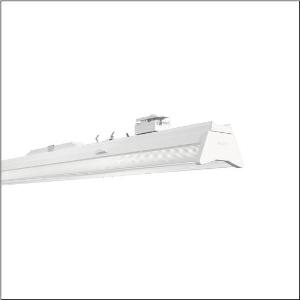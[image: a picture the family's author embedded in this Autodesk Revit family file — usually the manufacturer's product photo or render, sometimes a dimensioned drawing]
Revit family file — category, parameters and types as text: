
# Revit family: licross_r__21_performance_mo_52td16dn445g_3218
name_source: partatom
category: Lighting Fixtures
units: mm (PartAtom-declared; Revit-internal decimal feet)

## family parameters
Cut with Voids When Loaded = No
Host = Face
Light Source = No
Part Type = Normal
Room Calculation Point = No
Round Connector Dimension = Use Diameter
Shared = No

## types (1)
- --- (1 x LED, 4500 lm, 24.9 W, 4000K)
    Apparent Load = 25 VA
    CIE Flux Codes = 66 88 96 79 100
    Color Rendering = 80
    Color Temperature = 4000K
    Default Elevation = 1800 mm
    Description = Licross® 21 Performance MO, luminaire insert, of sheet steel, galvanised, coil coated, white, length: 1.500mm, width: 120mm, height: 123mm, LED rated luminous flux: 4.500lm, light colour: 840, SDCM (Standard Deviation of Colour Matching)MacAdam ≤ 3 SDCM (initial), control gear: DALI 2, with plug, 5-pole, with phase selection, mains connection: 220..240V, AC, 50/60Hz, rated input power: 25W, internal wiring halogen-free, primary light control with lens, of plastic, primary optical cover: cover, of PMMA, CAT 2 (L<= 3000cd/m²), light emission: direct/indirect distribution, primary light characteristic: symmetric, protection rating (complete): IP54, insulation class (complete): insulation class I (protective earthing), certification: CE, ENEC, VDE, UKCA, protection symbol: D if used in an environment with non-conductive dust loads with corresponding accessories, impact resistance: IK06, permissible ambient temperature for indoor applications: -25..+50°C, corresponds to IFS (International Featured Standards) requirements for safety and quality in the food industry, reducing of maximum allowable ambient temperature of 5°C with ceiling mounting, LABS conformity tested according to VDMA 24364:2018-05, packaging unit: 1 piece
    Height = 114 mm
    Lamp = 1 x LED
    Lamp Light Flux = 4500 lm
    Lamp Power = 24.9 W
    Lamp count = 1
    Length = 1500 mm
    Luminous efficacy = 181 lm/W
    Manufacturer = Siteco
    ModVariant = No
    Model = 52TD16DN445G
    Mounting Place = Ceiling
    Mounting Type = Pendant
    Number of Poles = 1
    OnlyDefault = Yes
    Power Factor = 1
    Product Name = Licross® 21 Performance MO
    Product group = luminaire insert | ceiling pendant
    ProductGroupID = 901
    Protection Class = Protection class I
    Protection Degree = IP 54
    RLX_Detail_Level = 1
    RLX_Emergency_Light_Flux = 0 lm
    RLX_Emergency_Type = 0
    RLX_Emergency_Type_DB = No
    RlxData = <blob elided: 33713 chars, md5=6601fcc0>
    Socket = socket
    Standby Power = 0 W
    System Light Flux = 4500 lm
    System Power = 25 W
    Type Comments = factory setting: luminous flux: 100 % | dim-lin: 254 | 165 mA
    Type Image = l_1256138.jpg
    URL = http://relux.com
    VarID = @adj_058747
    Voltage = 0 V
    Weight = 0.00 kg
    Width = 120 mm

## geometry (parser evidence)
native form markers: Blend x4, Sweep x14
no freeform markers — native parametric forms only
